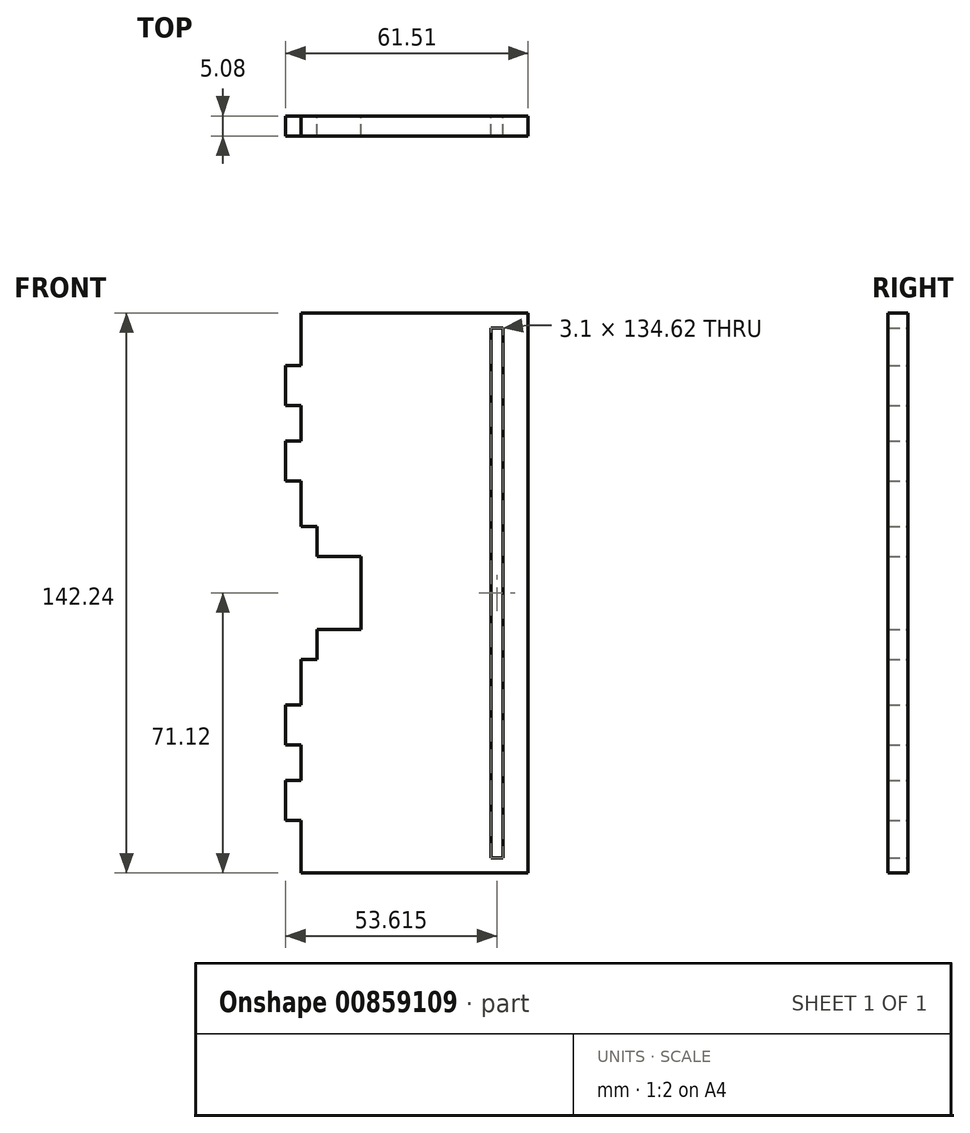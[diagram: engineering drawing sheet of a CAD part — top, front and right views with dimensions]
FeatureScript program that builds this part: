
annotation { "Feature Type Name" : "Feature", "Feature Type Description" : "" }
export const myFeature = defineFeature(function(context is Context, id is Id, definition is map)
    precondition{}
    {
        {
            var Q0;
            Q0=qCreatedBy(makeId("Front.planeOp"),FACE);
            var sketch = newSketch(context, id + "F0", { "sketchPlane" : qUnion([Q0])});
            skLineSegment(sketch, "E0.bottom", {"start": v(-28.85, 71.12) * mm, "end": v(28.85, 71.12) * mm});
            skLineSegment(sketch, "E0.top", {"start": v(-28.85, -71.12) * mm, "end": v(28.85, -71.12) * mm});
            skLineSegment(sketch, "E0.left", {"start": v(-28.85, 71.12) * mm, "end": v(-28.85, -71.12) * mm});
            skLineSegment(sketch, "E0.right", {"start": v(28.85, 71.12) * mm, "end": v(28.85, -71.12) * mm});
            skPoint(sketch, "E0.middle", {"position": v(0, 0) * mm});
            skLineSegment(sketch, "E1", {"start": v(0, 0) * mm, "end": v(-28.85, 0) * mm});
            skLineSegment(sketch, "E2", {"start": v(-28.85, 0) * mm, "end": v(-28.85, 28.47) * mm});
            skLineSegment(sketch, "E3.bottom", {"start": v(-28.85, 28.47) * mm, "end": v(-32.66, 28.47) * mm});
            skLineSegment(sketch, "E3.top", {"start": v(-28.85, 38.63) * mm, "end": v(-32.66, 38.63) * mm});
            skLineSegment(sketch, "E3.left", {"start": v(-28.85, 28.47) * mm, "end": v(-28.85, 38.63) * mm});
            skLineSegment(sketch, "E3.right", {"start": v(-32.66, 28.47) * mm, "end": v(-32.66, 38.63) * mm});
            skLineSegment(sketch, "E4", {"start": v(-28.85, 38.63) * mm, "end": v(-28.85, 47.63) * mm});
            skLineSegment(sketch, "E5.bottom", {"start": v(-28.85, 47.63) * mm, "end": v(-32.66, 47.63) * mm});
            skLineSegment(sketch, "E5.top", {"start": v(-28.85, 57.79) * mm, "end": v(-32.66, 57.79) * mm});
            skLineSegment(sketch, "E5.left", {"start": v(-28.85, 47.63) * mm, "end": v(-28.85, 57.79) * mm});
            skLineSegment(sketch, "E5.right", {"start": v(-32.66, 47.63) * mm, "end": v(-32.66, 57.79) * mm});
            skLineSegment(sketch, "E6.MirrorCS", {"start": v(-28.85, -28.47) * mm, "end": v(-32.66, -28.47) * mm});
            skLineSegment(sketch, "E7.MirrorCS", {"start": v(-32.66, -28.47) * mm, "end": v(-32.66, -38.63) * mm});
            skLineSegment(sketch, "E8.MirrorCS", {"start": v(-28.85, -38.63) * mm, "end": v(-32.66, -38.63) * mm});
            skLineSegment(sketch, "E9.MirrorCS", {"start": v(-28.85, -47.63) * mm, "end": v(-32.66, -47.63) * mm});
            skLineSegment(sketch, "E10.MirrorCS", {"start": v(-32.66, -47.63) * mm, "end": v(-32.66, -57.79) * mm});
            skLineSegment(sketch, "E11.MirrorCS", {"start": v(-28.85, -57.79) * mm, "end": v(-32.66, -57.79) * mm});
            skSolve(sketch);
        }
        {
            var Q0;
            Q0=qCreatedBy(makeId("Front.planeOp"),FACE);
            var sketch = newSketch(context, id + "F1", { "sketchPlane" : qUnion([Q0])});
            skLineSegment(sketch, "E12", {"start": v(0, 0) * mm, "end": v(22.5, 0) * mm});
            skLineSegment(sketch, "E13.bottom", {"start": v(22.5, 0) * mm, "end": v(19.4, 0) * mm});
            skLineSegment(sketch, "E13.top", {"start": v(22.5, 67.31) * mm, "end": v(19.4, 67.31) * mm});
            skLineSegment(sketch, "E13.left", {"start": v(22.5, 0) * mm, "end": v(22.5, 67.31) * mm});
            skLineSegment(sketch, "E13.right", {"start": v(19.4, 0) * mm, "end": v(19.4, 67.31) * mm});
            skLineSegment(sketch, "E14.MirrorCS", {"start": v(22.5, -67.31) * mm, "end": v(19.4, -67.31) * mm});
            skLineSegment(sketch, "E15.MirrorCS", {"start": v(19.4, 0) * mm, "end": v(19.4, -67.31) * mm});
            skLineSegment(sketch, "E16.MirrorCS", {"start": v(22.5, 0) * mm, "end": v(22.5, -67.31) * mm});
            skLineSegment(sketch, "E17", {"start": v(0, 0) * mm, "end": v(-21.23, 0) * mm});
            skPoint(sketch, "E18.middle", {"position": v(-21.23, 0) * mm});
            skLineSegment(sketch, "E19.bottom", {"start": v(-28.85, 9.27) * mm, "end": v(-13.61, 9.27) * mm});
            skLineSegment(sketch, "E19.top", {"start": v(-28.85, -9.27) * mm, "end": v(-13.61, -9.27) * mm});
            skLineSegment(sketch, "E19.left", {"start": v(-28.85, 9.27) * mm, "end": v(-28.85, -9.27) * mm});
            skLineSegment(sketch, "E19.right", {"start": v(-13.61, 9.27) * mm, "end": v(-13.61, -9.27) * mm});
            skLineSegment(sketch, "E20", {"start": v(-28.85, 0) * mm, "end": v(-26.82, 0) * mm});
            skLineSegment(sketch, "E21", {"start": v(-26.82, 0) * mm, "end": v(-26.82, 9.27) * mm});
            skLineSegment(sketch, "E22", {"start": v(-26.82, 9.27) * mm, "end": v(-26.82, 13.08) * mm});
            skLineSegment(sketch, "E23.bottom", {"start": v(-28.85, 9.27) * mm, "end": v(-24.8, 9.27) * mm});
            skLineSegment(sketch, "E23.top", {"start": v(-28.85, 16.9) * mm, "end": v(-24.8, 16.9) * mm});
            skLineSegment(sketch, "E23.left", {"start": v(-28.85, 9.27) * mm, "end": v(-28.85, 16.9) * mm});
            skLineSegment(sketch, "E23.right", {"start": v(-24.8, 9.27) * mm, "end": v(-24.8, 16.9) * mm});
            skPoint(sketch, "E23.middle", {"position": v(-26.82, 13.08) * mm});
            skLineSegment(sketch, "E24.MirrorCS", {"start": v(-28.85, -16.9) * mm, "end": v(-24.8, -16.9) * mm});
            skLineSegment(sketch, "E25.MirrorCS", {"start": v(-28.85, -9.27) * mm, "end": v(-28.85, -16.9) * mm});
            skLineSegment(sketch, "E26.MirrorCS", {"start": v(-24.8, -9.27) * mm, "end": v(-24.8, -16.9) * mm});
            skLineSegment(sketch, "E27.MirrorCS", {"start": v(-28.85, -9.27) * mm, "end": v(-24.8, -9.27) * mm});
            skSolve(sketch);
        }
        {
            var Q0;
            Q0 = qSketchRegion(id + "F0", true);
            extrude(context, id + "F2", {"entities" : qUnion([Q0]), "depth" : 5.08 * mm, "offsetDistance" : 25.4 * mm});
        }
        {
            var Q0;
            Q0 = qSketchRegion(id + "F1", true);
            extrude(context, id + "F3", {"entities" : qUnion([Q0]), "operationType" : NewBodyOperationType.REMOVE, "depth" : 33.27 * mm, "offsetDistance" : 25.4 * mm});
        }
    });
